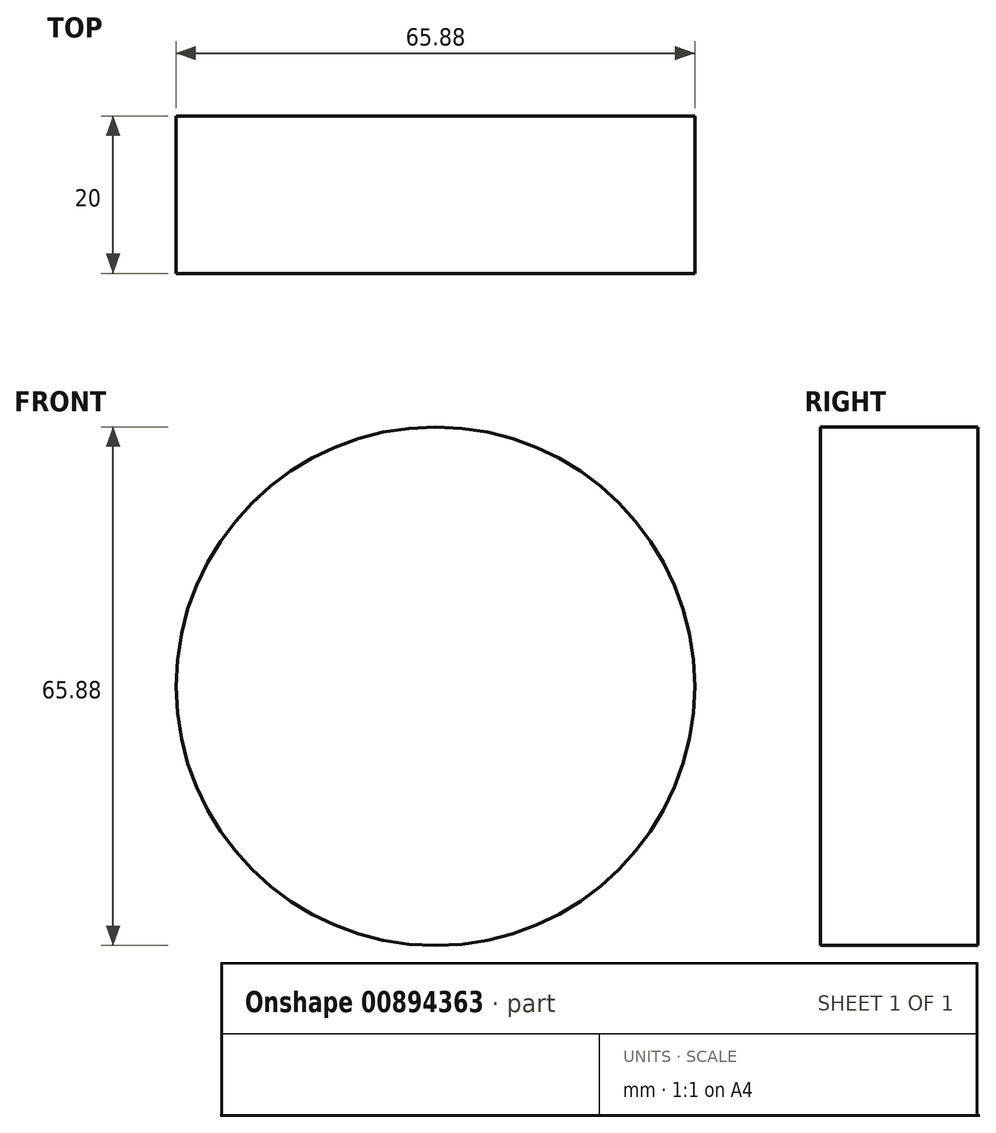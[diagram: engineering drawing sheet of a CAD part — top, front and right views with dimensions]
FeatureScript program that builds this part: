
annotation { "Feature Type Name" : "Feature", "Feature Type Description" : "" }
export const myFeature = defineFeature(function(context is Context, id is Id, definition is map)
    precondition{}
    {
        {
            var Q0;
            Q0=qCreatedBy(makeId("Front.planeOp"),FACE);
            var sketch = newSketch(context, id + "F0", { "sketchPlane" : qUnion([Q0])});
            skCircle(sketch, "E0", {"center": v(0, 0) * mm, "radius": 32.94 * mm});
            skSolve(sketch);
        }
        {
            var Q0;
            Q0 = qSketchRegion(id + "F0", true);
            extrude(context, id + "F1", {"entities" : qUnion([Q0]), "depth" : 20 * mm, "offsetDistance" : 25 * mm});
        }
    });
